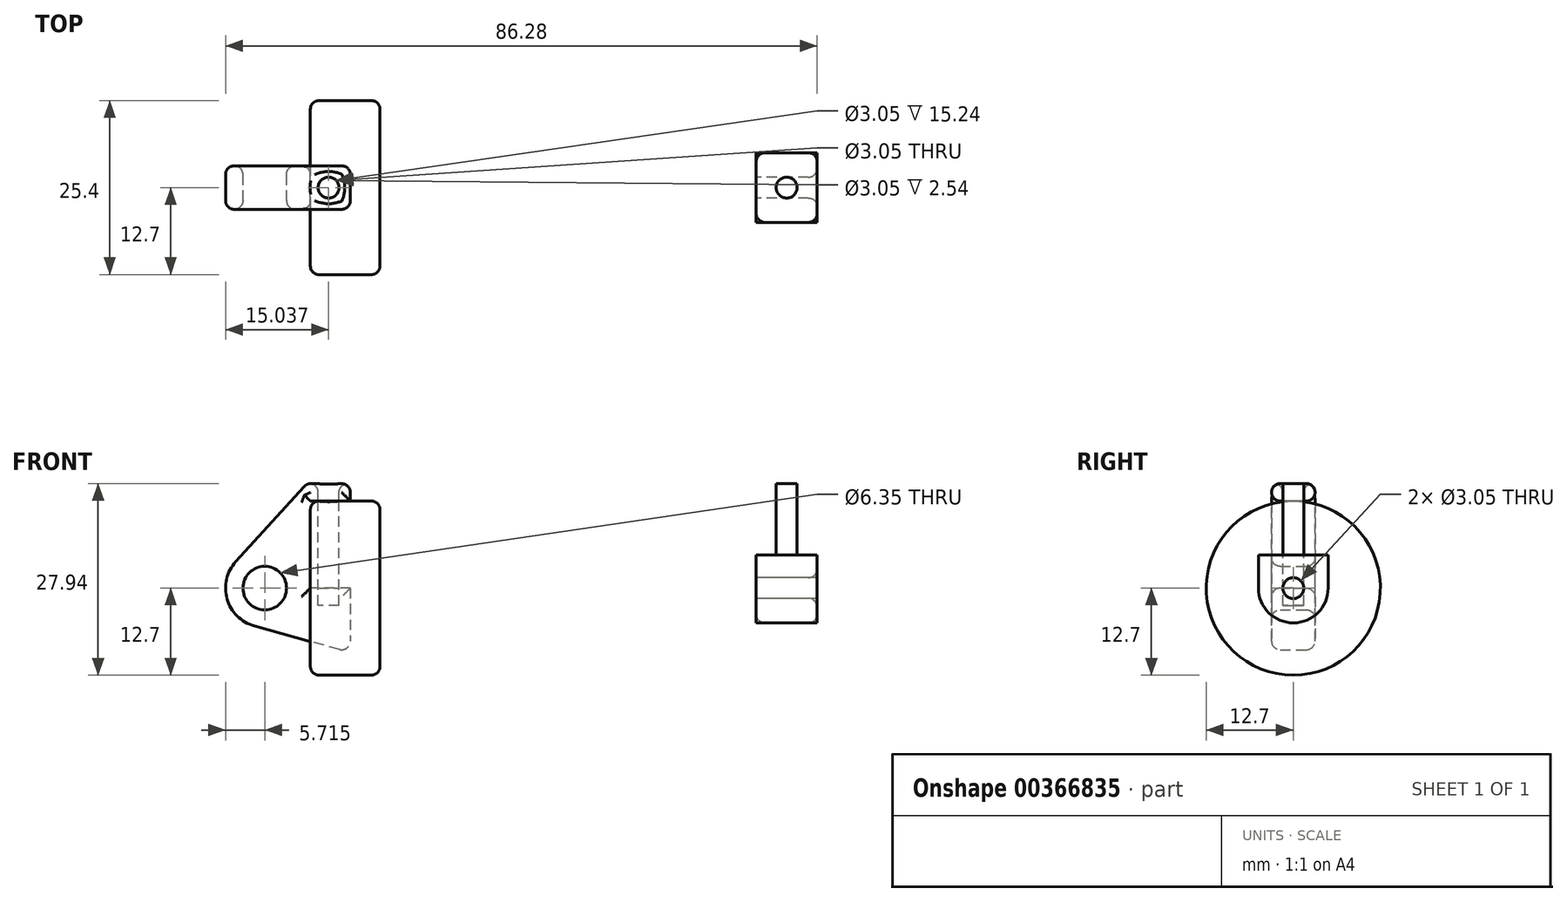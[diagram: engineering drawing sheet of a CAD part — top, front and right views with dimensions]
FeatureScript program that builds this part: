
annotation { "Feature Type Name" : "Feature", "Feature Type Description" : "" }
export const myFeature = defineFeature(function(context is Context, id is Id, definition is map)
    precondition{}
    {
        {
            var Q0;
            Q0=qCreatedBy(makeId("Front.planeOp"),FACE);
            var sketch = newSketch(context, id + "F0", { "sketchPlane" : qUnion([Q0])});
            skLineSegment(sketch, "E0", {"start": v(0, 0) * mm, "end": v(0, 12.7) * mm});
            skLineSegment(sketch, "E1", {"start": v(0, 12.7) * mm, "end": v(10.16, 12.7) * mm});
            skLineSegment(sketch, "E2", {"start": v(10.16, 12.7) * mm, "end": v(10.16, 10.16) * mm});
            skLineSegment(sketch, "E3", {"start": v(10.16, 10.16) * mm, "end": v(56.13, 10.16) * mm});
            skLineSegment(sketch, "E4", {"start": v(56.13, 10.16) * mm, "end": v(56.13, 12.7) * mm});
            skLineSegment(sketch, "E5", {"start": v(56.13, 12.7) * mm, "end": v(66.3, 12.7) * mm});
            skLineSegment(sketch, "E6", {"start": v(66.3, 12.7) * mm, "end": v(66.3, 0) * mm});
            skLineSegment(sketch, "E7", {"start": v(66.3, 0) * mm, "end": v(0, 0) * mm});
            skLineSegment(sketch, "E8", {"start": v(5.84, 15.24) * mm, "end": v(-0.5, 15.24) * mm});
            skLineSegment(sketch, "E9", {"start": v(-0.5, 15.24) * mm, "end": v(-10.88, 3.85) * mm});
            skLineSegment(sketch, "E10", {"start": v(0, 0) * mm, "end": v(-6.65, 0) * mm});
            skCircle(sketch, "E11", {"center": v(-6.65, 0) * mm, "radius": 5.72 * mm});
            skCircle(sketch, "E12", {"center": v(-6.65, 0) * mm, "radius": 3.18 * mm});
            skLineSegment(sketch, "E13", {"start": v(5.84, 15.24) * mm, "end": v(5.84, -9.4) * mm});
            skLineSegment(sketch, "E14", {"start": v(5.84, -9.4) * mm, "end": v(-8.18, -5.5) * mm});
            skLineSegment(sketch, "E15", {"start": v(0, 0) * mm, "end": v(0, -7.78) * mm});
            skLineSegment(sketch, "E16", {"start": v(10.16, 10.16) * mm, "end": v(10.16, 0) * mm});
            skSolve(sketch);
        }
        {
            var Q0;
            Q0=sQuery(id+"F0.wireOp",EDGE,"E3");
            var Q1;
            Q1=sQuery(id+"F0.wireOp",EDGE,"E5");
            var Q2;
            Q2=sQuery(id+"F0.wireOp",EDGE,"E6");
            var Q3;
            Q3=sQuery(id+"F0.wireOp",EDGE,"E4");
            var Q4;
            Q4=sQuery(id+"F0.wireOp",EDGE,"E7");
            revolve(context, id + "F1", {"bodyType" : ToolBodyType.SURFACE, "surfaceEntities" : qUnion([Q0, Q1, Q2, Q3]), "axis" : qUnion([Q4]), "revolveType" : RevolveType.FULL});
        }
        {
            var Q0;
            {var subQ1=sQuery(id+"F0.wireOp",EDGE,"E0");Q0=makeQuery(id+"F0.imprint","IMPRINT",FACE,{"disambiguationData":[TD([[makeQuery(id+"F0.imprint","IMPRINT",EDGE,{"derivedFrom":subQ1}),1.0]])]});}
            var Q1;
            {var subQ5=sQuery(id+"F0.wireOp",EDGE,"E12");Q1=makeQuery(id+"F0.imprint","IMPRINT",FACE,{"disambiguationData":[TD([[makeQuery(id+"F0.imprint","IMPRINT",EDGE,{"derivedFrom":subQ5}),-1.0]])]});}
            var Q2;
            {var subQ0=sQuery(id+"F0.wireOp",EDGE,"E14");Q2=makeQuery(id+"F0.imprint","IMPRINT",FACE,{"disambiguationData":[TD([[makeQuery(id+"F0.imprint","IMPRINT",EDGE,{"derivedFrom":subQ0}),-1.0]])]});}
            extrude(context, id + "F2", {"entities" : qUnion([Q0, Q1, Q2]), "depth" : 3.17 * mm});
        }
        {
            var Q0;
            {var subQ1=sQuery(id+"F0.wireOp",EDGE,"E0");Q0=makeQuery(id+"F0.imprint","IMPRINT",FACE,{"disambiguationData":[TD([[makeQuery(id+"F0.imprint","IMPRINT",EDGE,{"derivedFrom":subQ1}),1.0]])]});}
            var Q1;
            {var subQ5=sQuery(id+"F0.wireOp",EDGE,"E12");Q1=makeQuery(id+"F0.imprint","IMPRINT",FACE,{"disambiguationData":[TD([[makeQuery(id+"F0.imprint","IMPRINT",EDGE,{"derivedFrom":subQ5}),-1.0]])]});}
            var Q2;
            {var subQ0=sQuery(id+"F0.wireOp",EDGE,"E14");Q2=makeQuery(id+"F0.imprint","IMPRINT",FACE,{"disambiguationData":[TD([[makeQuery(id+"F0.imprint","IMPRINT",EDGE,{"derivedFrom":subQ0}),-1.0]])]});}
            extrude(context, id + "F3", {"entities" : qUnion([Q0, Q1, Q2]), "operationType" : NewBodyOperationType.ADD, "oppositeDirection" : true, "depth" : 3.17 * mm});
        }
        {
            var Q0;
            Q0=makeQuery(id+"F1.opRevolve","SWEPT_FACE",FACE,{"disambiguationData":[OSD([sQuery(id+"F0.wireOp",EDGE,"E6")])]});
            var sketch = newSketch(context, id + "F4", { "sketchPlane" : qUnion([Q0])});
            skCircle(sketch, "E17", {"center": v(0, 0) * mm, "radius": 1.52 * mm});
            skCircle(sketch, "E18", {"center": v(0, 0) * mm, "radius": 5.08 * mm});
            skLineSegment(sketch, "E19", {"start": v(-5.08, 0) * mm, "end": v(-5.08, 15.24) * mm});
            skLineSegment(sketch, "E20", {"start": v(5.08, 0) * mm, "end": v(5.08, 15.24) * mm});
            skLineSegment(sketch, "E21", {"start": v(5.08, 15.24) * mm, "end": v(-5.08, 15.24) * mm});
            skSolve(sketch);
        }
        {
            var Q0;
            {var subQ0=sQuery(id+"F4.wireOp",EDGE,"E21");Q0=makeQuery(id+"F4.imprint","IMPRINT",FACE,{"disambiguationData":[TD([[makeQuery(id+"F4.imprint","IMPRINT",EDGE,{"derivedFrom":subQ0}),1.0]])]});}
            var Q1;
            {var subQ0=sQuery(id+"F4.wireOp",EDGE,"E19");var subQ1=sQuery(id+"F4.wireOp",EDGE,"E18");var subQ2=makeQuery(id+"F4.imprint","INTERSECT",VERTEX,{"derivedFrom":[subQ1,subQ0]});Q1=makeQuery(id+"F4.imprint","IMPRINT",FACE,{"disambiguationData":[TD([[makeQuery(id+"F4.imprint","IMPRINT",EDGE,{"disambiguationData":[TD([[subQ2,1.0]])],"derivedFrom":subQ1}),-1.0]])]});}
            var Q2;
            Q2=makeQuery(id+"F4.imprint","IMPRINT",FACE,{"disambiguationData":[TD([[makeQuery(id+"F4.imprint","IMPRINT",EDGE,{"derivedFrom":sQuery(id+"F4.wireOp",EDGE,"E17")}),-1.0]])]});
            extrude(context, id + "F5", {"entities" : qUnion([Q0, Q1, Q2]), "depth" : 7.62 * mm, "hasSecondDirection" : true, "secondDirectionOppositeDirection" : true, "secondDirectionDepth" : 1.27 * mm});
        }
        {
            var Q0;
            Q0=makeQuery(id+"F5.opExtrude","SWEPT_FACE",FACE,{"disambiguationData":[OSD([sQuery(id+"F4.wireOp",EDGE,"E21")])]});
            var sketch = newSketch(context, id + "F6", { "sketchPlane" : qUnion([Q0])});
            skLineSegment(sketch, "E22", {"start": v(69.47, 5.08) * mm, "end": v(69.47, -5.08) * mm});
            skCircle(sketch, "E23", {"center": v(69.47, 0) * mm, "radius": 1.52 * mm});
            skSolve(sketch);
        }
        {
            var Q0;
            Q0 = qSketchRegion(id + "F6", true);
            extrude(context, id + "F7", {"entities" : qUnion([Q0]), "operationType" : NewBodyOperationType.REMOVE, "oppositeDirection" : true, "depth" : 10.4 * mm});
        }
        {
            var Q0;
            {var subQ0=sQuery(id+"F0.wireOp",EDGE,"E8");Q0=makeQuery(id+"F3.boolean.opBoolean","MERGE",FACE,{"derivedFrom":[makeQuery(id+"F2.opExtrude","SWEPT_FACE",FACE,{"disambiguationData":[OSD([subQ0])]}),makeQuery(id+"F3.opExtrude","SWEPT_FACE",FACE,{"disambiguationData":[OSD([subQ0])]})]});}
            var sketch = newSketch(context, id + "F8", { "sketchPlane" : qUnion([Q0])});
            skCircle(sketch, "E24", {"center": v(2.67, 0) * mm, "radius": 1.52 * mm});
            skPoint(sketch, "E24.centerSnap0", {"position": v(5.84, 0) * mm});
            skPoint(sketch, "E24.centerSnap1", {"position": v(2.67, 3.18) * mm});
            skSolve(sketch);
        }
        {
            var Q0;
            Q0=makeQuery(id+"F8.imprint","IMPRINT",FACE,{"disambiguationData":[TD([[makeQuery(id+"F8.imprint","IMPRINT",EDGE,{"derivedFrom":sQuery(id+"F8.wireOp",EDGE,"E24")}),1.0]])]});
            extrude(context, id + "F9", {"entities" : qUnion([Q0]), "operationType" : NewBodyOperationType.REMOVE, "oppositeDirection" : true, "depth" : 17.78 * mm});
        }
        {
            var Q0;
            Q0=makeQuery(id+"F2.opExtrude","CAP_FACE",FACE,{"disambiguationData":[OSD([sQuery(id+"F0.wireOp",EDGE,"E0"),sQuery(id+"F0.wireOp",EDGE,"E1"),sQuery(id+"F0.wireOp",EDGE,"E7"),sQuery(id+"F0.wireOp",EDGE,"E8"),sQuery(id+"F0.wireOp",EDGE,"E9"),sQuery(id+"F0.wireOp",EDGE,"E11"),sQuery(id+"F0.wireOp",EDGE,"E12"),sQuery(id+"F0.wireOp",EDGE,"E13"),sQuery(id+"F0.wireOp",EDGE,"E14")])],"isStart":false});
            var Q1;
            Q1=makeQuery(id+"F3.opExtrude","CAP_FACE",FACE,{"disambiguationData":[OSD([sQuery(id+"F0.wireOp",EDGE,"E0"),sQuery(id+"F0.wireOp",EDGE,"E1"),sQuery(id+"F0.wireOp",EDGE,"E7"),sQuery(id+"F0.wireOp",EDGE,"E8"),sQuery(id+"F0.wireOp",EDGE,"E9"),sQuery(id+"F0.wireOp",EDGE,"E11"),sQuery(id+"F0.wireOp",EDGE,"E12"),sQuery(id+"F0.wireOp",EDGE,"E13"),sQuery(id+"F0.wireOp",EDGE,"E14")])],"isStart":false});
            var Q2;
            {var subQ0=sQuery(id+"F0.wireOp",EDGE,"E8");Q2=makeQuery(id+"F3.boolean.opBoolean","MERGE",FACE,{"derivedFrom":[makeQuery(id+"F2.opExtrude","SWEPT_FACE",FACE,{"disambiguationData":[OSD([subQ0])]}),makeQuery(id+"F3.opExtrude","SWEPT_FACE",FACE,{"disambiguationData":[OSD([subQ0])]})]});}
            var Q3;
            {var subQ0=sQuery(id+"F0.wireOp",EDGE,"E11");Q3=makeQuery(id+"F3.boolean.opBoolean","MERGE",FACE,{"derivedFrom":[makeQuery(id+"F2.opExtrude","SWEPT_FACE",FACE,{"disambiguationData":[OSD([subQ0])]}),makeQuery(id+"F3.opExtrude","SWEPT_FACE",FACE,{"disambiguationData":[OSD([subQ0])]})]});}
            var Q4;
            {var subQ0=sQuery(id+"F0.wireOp",EDGE,"E14");Q4=makeQuery(id+"F3.boolean.opBoolean","MERGE",FACE,{"derivedFrom":[makeQuery(id+"F2.opExtrude","SWEPT_FACE",FACE,{"disambiguationData":[OSD([subQ0])]}),makeQuery(id+"F3.opExtrude","SWEPT_FACE",FACE,{"disambiguationData":[OSD([subQ0])]})]});}
            var Q5;
            Q5=makeQuery(id+"F1.opRevolve","SWEPT_FACE",FACE,{"disambiguationData":[OSD([sQuery(id+"F0.wireOp",EDGE,"E0")])]});
            var Q6;
            Q6=makeQuery(id+"F1.opRevolve","SWEPT_FACE",FACE,{"disambiguationData":[OSD([sQuery(id+"F0.wireOp",EDGE,"E1")])]});
            var Q7;
            Q7=makeQuery(id+"F1.opRevolve","SWEPT_EDGE",EDGE,{"disambiguationData":[OSD([sQuery(id+"F0.wireOp",VERTEX,"E2.end")])]});
            var Q8;
            Q8=makeQuery(id+"F1.opRevolve","SWEPT_FACE",FACE,{"disambiguationData":[OSD([sQuery(id+"F0.wireOp",EDGE,"E3")])]});
            var Q9;
            Q9=makeQuery(id+"F1.opRevolve","SWEPT_EDGE",EDGE,{"disambiguationData":[OSD([sQuery(id+"F0.wireOp",VERTEX,"E4.end")])]});
            var Q10;
            Q10=makeQuery(id+"F1.opRevolve","SWEPT_FACE",FACE,{"disambiguationData":[OSD([sQuery(id+"F0.wireOp",EDGE,"E5")])]});
            var Q11;
            Q11=makeQuery(id+"F1.opRevolve","SWEPT_FACE",FACE,{"disambiguationData":[OSD([sQuery(id+"F0.wireOp",EDGE,"E6")])]});
            fillet(context, id + "F10", {"entities" : qUnion([Q0, Q1, Q2, Q3, Q4, Q5, Q6, Q7, Q8, Q9, Q10, Q11]), "radius" : 1.27 * mm, "tangentPropagation" : true, "allowEdgeOverflow" : false});
        }
        {
            var Q0;
            {var subQ0=sQuery(id+"F4.wireOp",EDGE,"E19");var subQ1=sQuery(id+"F4.wireOp",EDGE,"E18");var subQ2=makeQuery(id+"F4.imprint","INTERSECT",VERTEX,{"derivedFrom":[subQ1,subQ0]});Q0=makeQuery(id+"F4.imprint","IMPRINT",FACE,{"disambiguationData":[TD([[makeQuery(id+"F4.imprint","IMPRINT",EDGE,{"disambiguationData":[TD([[subQ2,1.0]])],"derivedFrom":subQ1}),-1.0]])]});}
            var Q1;
            Q1=makeQuery(id+"F4.imprint","IMPRINT",FACE,{"disambiguationData":[TD([[makeQuery(id+"F4.imprint","IMPRINT",EDGE,{"derivedFrom":sQuery(id+"F4.wireOp",EDGE,"E17")}),-1.0]])]});
            var Q2;
            {var subQ0=sQuery(id+"F4.wireOp",EDGE,"E21");Q2=makeQuery(id+"F4.imprint","IMPRINT",FACE,{"disambiguationData":[TD([[makeQuery(id+"F4.imprint","IMPRINT",EDGE,{"derivedFrom":subQ0}),1.0]])]});}
            var Q3;
            Q3=sQuery(id+"F4.wireOp",EDGE,"E19");
            var Q4;
            Q4=sQuery(id+"F4.wireOp",EDGE,"E20");
            var Q5;
            Q5=sQuery(id+"F4.wireOp",EDGE,"E18");
            var Q6;
            Q6=sQuery(id+"F4.wireOp",EDGE,"E21");
            extrude(context, id + "F11", {"entities" : qUnion([Q0, Q1, Q2]), "surfaceEntities" : qUnion([Q3, Q4, Q5, Q6]), "depth" : 7.62 * mm, "hasSecondDirection" : true, "secondDirectionOppositeDirection" : true, "secondDirectionDepth" : 1.27 * mm});
        }
        {
            var Q0;
            Q0=makeQuery(id+"F11.opExtrude","CAP_FACE",FACE,{"disambiguationData":[OSD([sQuery(id+"F4.wireOp",EDGE,"E17"),sQuery(id+"F4.wireOp",EDGE,"E18"),sQuery(id+"F4.wireOp",EDGE,"E19"),sQuery(id+"F4.wireOp",EDGE,"E20"),sQuery(id+"F4.wireOp",EDGE,"E21")])],"isStart":false});
            var Q1;
            Q1=makeQuery(id+"F11.opExtrude","SWEPT_FACE",FACE,{"disambiguationData":[OSD([sQuery(id+"F4.wireOp",EDGE,"E21")])]});
            var Q2;
            Q2=makeQuery(id+"F11.opExtrude","SWEPT_FACE",FACE,{"disambiguationData":[OSD([sQuery(id+"F4.wireOp",EDGE,"E20")])]});
            fillet(context, id + "F12", {"entities" : qUnion([Q0, Q1, Q2]), "radius" : 1.27 * mm, "tangentPropagation" : true, "allowEdgeOverflow" : false});
        }
        {
            var Q0;
            {var subQ0=sQuery(id+"F6.wireOp",EDGE,"E23");var subQ1=sQuery(id+"F6.wireOp",EDGE,"E22");var subQ2=makeQuery(id+"F6.imprint","INTERSECT",VERTEX,{"disambiguationData":[OD(0.0)],"derivedFrom":[subQ1,subQ0]});Q0=makeQuery(id+"F6.imprint","IMPRINT",FACE,{"disambiguationData":[TD([[makeQuery(id+"F6.imprint","IMPRINT",EDGE,{"disambiguationData":[TD([[subQ2,-1.0]])],"derivedFrom":subQ1}),-1.0]])]});}
            var Q1;
            {var subQ0=sQuery(id+"F6.wireOp",EDGE,"E23");var subQ1=sQuery(id+"F6.wireOp",EDGE,"E22");var subQ2=makeQuery(id+"F6.imprint","INTERSECT",VERTEX,{"disambiguationData":[OD(0.0)],"derivedFrom":[subQ1,subQ0]});Q1=makeQuery(id+"F6.imprint","IMPRINT",FACE,{"disambiguationData":[TD([[makeQuery(id+"F6.imprint","IMPRINT",EDGE,{"disambiguationData":[TD([[subQ2,-1.0]])],"derivedFrom":subQ1}),1.0]])]});}
            var Q2;
            Q2=sQuery(id+"F6.wireOp",EDGE,"E23");
            extrude(context, id + "F13", {"entities" : qUnion([Q0, Q1]), "operationType" : NewBodyOperationType.REMOVE, "surfaceEntities" : qUnion([Q2]), "oppositeDirection" : true, "depth" : 10.4 * mm});
        }
        {
            var Q0;
            Q0 = qSketchRegion(id + "F8", true);
            extrude(context, id + "F14", {"entities" : qUnion([Q0]), "operationType" : NewBodyOperationType.REMOVE, "oppositeDirection" : true, "depth" : 17.78 * mm});
        }
        {
            var Q0;
            {var subQ0=sQuery(id+"F0.wireOp",EDGE,"E0");Q0=makeQuery(id+"F0.imprint","IMPRINT",FACE,{"disambiguationData":[TD([[makeQuery(id+"F0.imprint","IMPRINT",EDGE,{"derivedFrom":subQ0}),-1.0]])]});}
            var Q1;
            {var subQ6=sQuery(id+"F0.wireOp",EDGE,"E2");Q1=makeQuery(id+"F0.imprint","IMPRINT",FACE,{"disambiguationData":[TD([[makeQuery(id+"F0.imprint","IMPRINT",EDGE,{"derivedFrom":subQ6}),-1.0]])]});}
            var Q2;
            Q2=sQuery(id+"F0.wireOp",EDGE,"E7");
            revolve(context, id + "F15", {"entities" : qUnion([Q0, Q1]), "axis" : qUnion([Q2]), "revolveType" : RevolveType.FULL});
        }
        {
            var Q0;
            Q0=makeQuery(id+"F8.imprint","IMPRINT",FACE,{"disambiguationData":[TD([[makeQuery(id+"F8.imprint","IMPRINT",EDGE,{"derivedFrom":sQuery(id+"F8.wireOp",EDGE,"E24")}),1.0]])]});
            var Q1;
            Q1=sQuery(id+"F8.wireOp",EDGE,"E24");
            extrude(context, id + "F16", {"entities" : qUnion([Q0]), "operationType" : NewBodyOperationType.REMOVE, "surfaceEntities" : qUnion([Q1]), "oppositeDirection" : true, "depth" : 17.78 * mm});
        }
        {
            var Q0;
            Q0=makeQuery(id+"F15.opRevolve","SWEPT_EDGE",EDGE,{"disambiguationData":[OSD([sQuery(id+"F0.wireOp",EDGE,"E1"),sQuery(id+"F0.wireOp",EDGE,"E2")])]});
            var Q1;
            Q1=makeQuery(id+"F15.opRevolve","SWEPT_FACE",FACE,{"disambiguationData":[OSD([sQuery(id+"F0.wireOp",EDGE,"E0")])]});
            fillet(context, id + "F17", {"entities" : qUnion([Q0, Q1]), "radius" : 1.27 * mm, "tangentPropagation" : true, "allowEdgeOverflow" : false});
        }
    });
